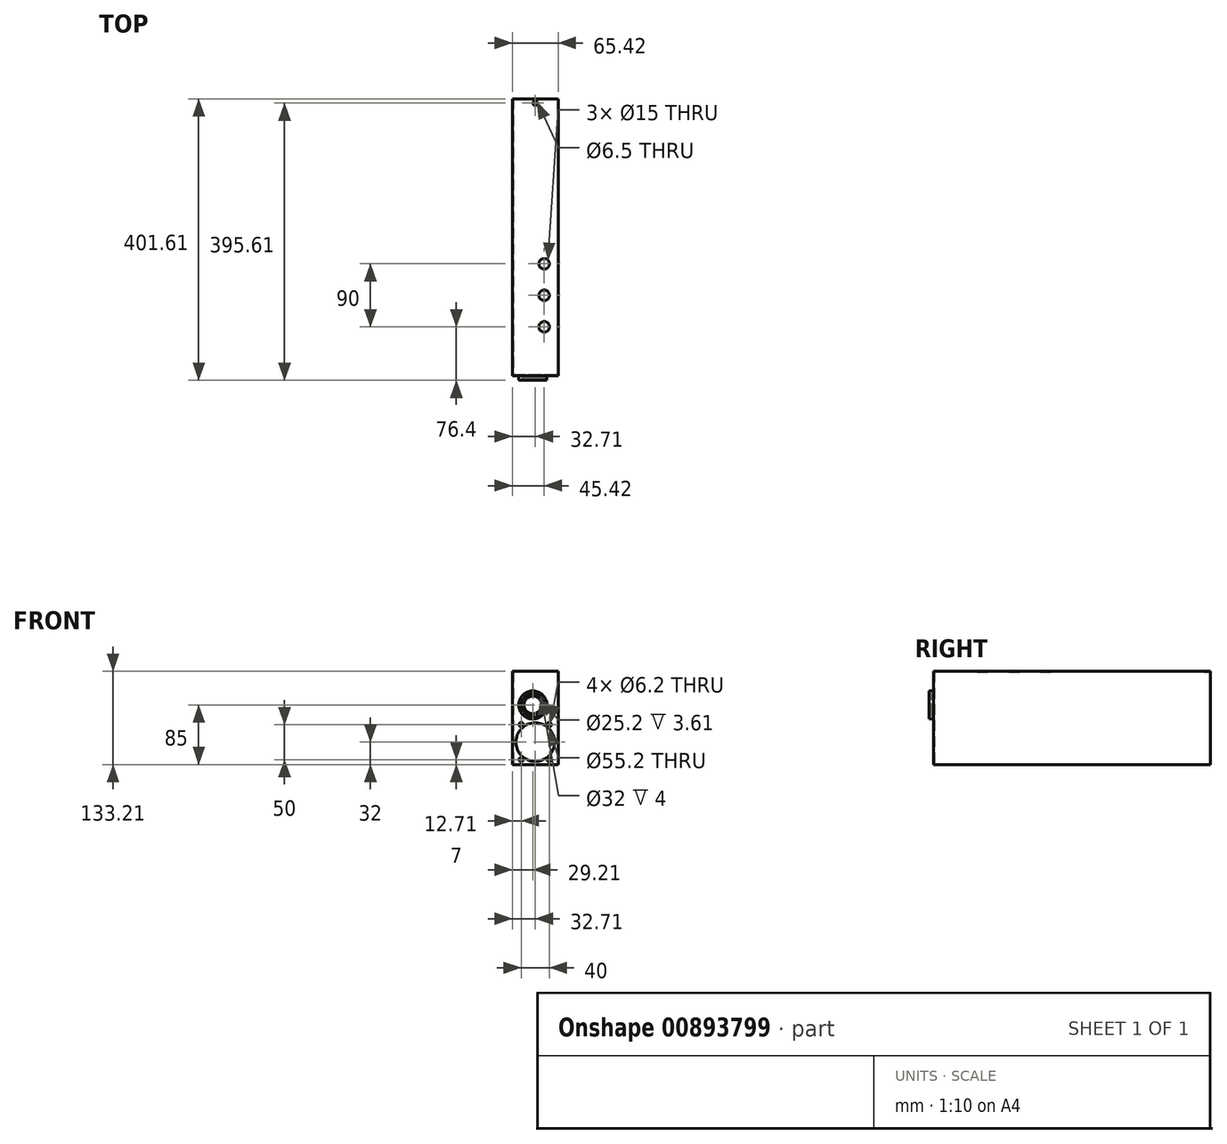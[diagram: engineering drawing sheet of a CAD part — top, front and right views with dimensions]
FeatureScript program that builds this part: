
annotation { "Feature Type Name" : "Feature", "Feature Type Description" : "" }
export const myFeature = defineFeature(function(context is Context, id is Id, definition is map)
    precondition{}
    {
        {
            var Q0;
            Q0=qCreatedBy(makeId("Front.planeOp"),FACE);
            var sketch = newSketch(context, id + "F0", { "sketchPlane" : qUnion([Q0])});
            skLineSegment(sketch, "E0", {"start": v(0, 132) * mm, "end": v(-31.5, 132) * mm});
            skLineSegment(sketch, "E1", {"start": v(-31.5, 132) * mm, "end": v(-31.5, 0) * mm});
            skLineSegment(sketch, "E2", {"start": v(-31.5, 0) * mm, "end": v(-32.7, 0) * mm});
            skLineSegment(sketch, "E3", {"start": v(-32.7, 0) * mm, "end": v(-32.7, 133.21) * mm});
            skLineSegment(sketch, "E4", {"start": v(-32.7, 133.21) * mm, "end": v(0, 133.21) * mm});
            skLineSegment(sketch, "E5", {"start": v(0, 30.11) * mm, "end": v(0, -5.7) * mm, "construction": true});
            skLineSegment(sketch, "E6.MirrorCS", {"start": v(31.5, 0) * mm, "end": v(32.7, 0) * mm});
            skLineSegment(sketch, "E7.MirrorCS", {"start": v(0, 132) * mm, "end": v(31.5, 132) * mm});
            skLineSegment(sketch, "E8.MirrorCS", {"start": v(31.5, 132) * mm, "end": v(31.5, 0) * mm});
            skLineSegment(sketch, "E9.MirrorCS", {"start": v(32.7, 133.21) * mm, "end": v(0, 133.21) * mm});
            skLineSegment(sketch, "E10.MirrorCS", {"start": v(32.7, 0) * mm, "end": v(32.7, 133.21) * mm});
            skSolve(sketch);
        }
        {
            var Q0;
            Q0 = qSketchRegion(id + "F0", true);
            extrude(context, id + "F1", {"entities" : qUnion([Q0]), "oppositeDirection" : true, "depth" : (394) * mm, "offsetDistance" : 25 * mm});
        }
        {
            var Q0;
            Q0=makeQuery(id+"F1.opExtrude","CAP_FACE",FACE,{"disambiguationData":[OSD([sQuery(id+"F0.wireOp",EDGE,"E0"),sQuery(id+"F0.wireOp",EDGE,"E1"),sQuery(id+"F0.wireOp",EDGE,"E2"),sQuery(id+"F0.wireOp",EDGE,"E3"),sQuery(id+"F0.wireOp",EDGE,"E4"),sQuery(id+"F0.wireOp",EDGE,"E6.MirrorCS"),sQuery(id+"F0.wireOp",EDGE,"E7.MirrorCS"),sQuery(id+"F0.wireOp",EDGE,"E8.MirrorCS"),sQuery(id+"F0.wireOp",EDGE,"E9.MirrorCS"),sQuery(id+"F0.wireOp",EDGE,"E10.MirrorCS")])],"isStart":true});
            var sketch = newSketch(context, id + "F2", { "sketchPlane" : qUnion([Q0])});
            skLineSegment(sketch, "E11.0", {"start": v(32.71, 0) * mm, "end": v(-32.7, 0) * mm});
            skLineSegment(sketch, "E12.0", {"start": v(-32.7, 0) * mm, "end": v(-32.7, 133.21) * mm});
            skLineSegment(sketch, "E13.0", {"start": v(32.7, 133.21) * mm, "end": v(-32.7, 133.21) * mm});
            skLineSegment(sketch, "E14.0", {"start": v(32.7, 0) * mm, "end": v(32.7, 133.21) * mm});
            skPoint(sketch, "E15.orphan", {"position": v(-31.5, 0) * mm});
            skSolve(sketch);
        }
        {
            var Q0;
            Q0 = qSketchRegion(id + "F2", true);
            extrude(context, id + "F3", {"entities" : qUnion([Q0]), "operationType" : NewBodyOperationType.ADD, "depth" : 1.21 * mm, "offsetDistance" : 25 * mm});
        }
        {
            var Q0;
            Q0=makeQuery(id+"F3.opExtrude","CAP_FACE",FACE,{"disambiguationData":[OSD([sQuery(id+"F2.wireOp",EDGE,"E11.0"),sQuery(id+"F2.wireOp",EDGE,"E12.0"),sQuery(id+"F2.wireOp",EDGE,"E13.0"),sQuery(id+"F2.wireOp",EDGE,"E14.0")])],"isStart":false});
            var sketch = newSketch(context, id + "F4", { "sketchPlane" : qUnion([Q0])});
            skCircle(sketch, "E16", {"center": v(0, 32) * mm, "radius": 27.6 * mm});
            skSolve(sketch);
        }
        {
            var Q0;
            Q0 = qSketchRegion(id + "F4", true);
            extrude(context, id + "F5", {"entities" : qUnion([Q0]), "operationType" : NewBodyOperationType.REMOVE, "endBound" : BoundingType.THROUGH_ALL, "oppositeDirection" : true, "depth" : 25 * mm, "offsetDistance" : 25 * mm});
        }
        {
            var Q0;
            Q0=makeQuery(id+"F3.opExtrude","CAP_FACE",FACE,{"disambiguationData":[OSD([sQuery(id+"F2.wireOp",EDGE,"E11.0"),sQuery(id+"F2.wireOp",EDGE,"E12.0"),sQuery(id+"F2.wireOp",EDGE,"E13.0"),sQuery(id+"F2.wireOp",EDGE,"E14.0")])],"isStart":false});
            var sketch = newSketch(context, id + "F6", { "sketchPlane" : qUnion([Q0])});
            skCircle(sketch, "E17", {"center": v(-3.5, 85) * mm, "radius": 12.6 * mm});
            skPoint(sketch, "E17.centerSnap0", {"position": v(0, 133.21) * mm});
            skCircle(sketch, "E18.0", {"center": v(0, 32) * mm, "radius": 27.6 * mm, "construction": true});
            skSolve(sketch);
        }
        {
            var Q0;
            Q0 = qSketchRegion(id + "F6", true);
            extrude(context, id + "F7", {"entities" : qUnion([Q0]), "operationType" : NewBodyOperationType.REMOVE, "endBound" : BoundingType.THROUGH_ALL, "oppositeDirection" : true, "depth" : 25 * mm, "offsetDistance" : 25 * mm, "hasSecondDirection" : true, "secondDirectionBound" : SecondDirectionBoundingType.THROUGH_ALL, "secondDirectionOppositeDirection" : false, "secondDirectionDepth" : 25 * mm});
        }
        {
            var Q0;
            Q0=makeQuery(id+"F3.opExtrude","CAP_FACE",FACE,{"disambiguationData":[OSD([sQuery(id+"F2.wireOp",EDGE,"E11.0"),sQuery(id+"F2.wireOp",EDGE,"E12.0"),sQuery(id+"F2.wireOp",EDGE,"E13.0"),sQuery(id+"F2.wireOp",EDGE,"E14.0")])],"isStart":false});
            var sketch = newSketch(context, id + "F8", { "sketchPlane" : qUnion([Q0])});
            skCircle(sketch, "E19.0", {"center": v(-3.5, 85) * mm, "radius": 12.6 * mm});
            skCircle(sketch, "E20", {"center": v(-3.5, 85) * mm, "radius": 20 * mm});
            skSolve(sketch);
        }
        {
            var Q0;
            Q0 = qSketchRegion(id + "F8", true);
            extrude(context, id + "F9", {"entities" : qUnion([Q0]), "operationType" : NewBodyOperationType.ADD, "depth" : 6.4 * mm, "offsetDistance" : 25 * mm});
        }
        {
            var Q0;
            Q0=makeQuery(id+"F9.opExtrude","CAP_FACE",FACE,{"disambiguationData":[OSD([sQuery(id+"F8.wireOp",EDGE,"E19.0"),sQuery(id+"F8.wireOp",EDGE,"E20")])],"isStart":false});
            var sketch = newSketch(context, id + "F10", { "sketchPlane" : qUnion([Q0])});
            skCircle(sketch, "E21", {"center": v(-3.5, 85) * mm, "radius": 16 * mm});
            skSolve(sketch);
        }
        {
            var Q0;
            Q0=makeQuery(id+"F3.boolean.opBoolean","MERGE",FACE,{"derivedFrom":[makeQuery(id+"F1.opExtrude","SWEPT_FACE",FACE,{"disambiguationData":[OSD([sQuery(id+"F0.wireOp",EDGE,"E4"),sQuery(id+"F0.wireOp",EDGE,"E9.MirrorCS")])]}),makeQuery(id+"F3.opExtrude","SWEPT_FACE",FACE,{"disambiguationData":[OSD([sQuery(id+"F2.wireOp",EDGE,"E13.0")])]})]});
            var sketch = newSketch(context, id + "F11", { "sketchPlane" : qUnion([Q0])});
            skCircle(sketch, "E22", {"center": v(12.7, 68.8) * mm, "radius": 7.5 * mm});
            skCircle(sketch, "E23", {"center": v(12.7, 113.8) * mm, "radius": 7.5 * mm});
            skCircle(sketch, "E24", {"center": v(12.7, 158.79) * mm, "radius": 7.5 * mm});
            skSolve(sketch);
        }
        {
            var Q0;
            Q0 = qSketchRegion(id + "F11", true);
            extrude(context, id + "F12", {"entities" : qUnion([Q0]), "operationType" : NewBodyOperationType.REMOVE, "endBound" : BoundingType.THROUGH_ALL, "oppositeDirection" : true, "depth" : 25 * mm, "offsetDistance" : 25 * mm});
        }
        {
            var Q0;
            Q0=makeQuery(id+"F3.boolean.opBoolean","MERGE",FACE,{"derivedFrom":[makeQuery(id+"F1.opExtrude","SWEPT_FACE",FACE,{"disambiguationData":[OSD([sQuery(id+"F0.wireOp",EDGE,"E4"),sQuery(id+"F0.wireOp",EDGE,"E9.MirrorCS")])]}),makeQuery(id+"F3.opExtrude","SWEPT_FACE",FACE,{"disambiguationData":[OSD([sQuery(id+"F2.wireOp",EDGE,"E13.0")])]})]});
            var sketch = newSketch(context, id + "F13", { "sketchPlane" : qUnion([Q0])});
            skCircle(sketch, "E25", {"center": v(0, 388) * mm, "radius": 3.25 * mm});
            skLineSegment(sketch, "E26", {"start": v(0, 0) * mm, "end": v(0, 401.41) * mm, "construction": true});
            skSolve(sketch);
        }
        {
            var Q0;
            Q0 = qSketchRegion(id + "F13", true);
            extrude(context, id + "F14", {"entities" : qUnion([Q0]), "operationType" : NewBodyOperationType.REMOVE, "oppositeDirection" : true, "depth" : 25 * mm, "offsetDistance" : 25 * mm});
        }
        {
            var Q0;
            Q0 = qSketchRegion(id + "F10", true);
            extrude(context, id + "F15", {"entities" : qUnion([Q0]), "operationType" : NewBodyOperationType.REMOVE, "oppositeDirection" : true, "depth" : 4 * mm, "offsetDistance" : 25 * mm});
        }
        {
            var Q0;
            Q0=makeQuery(id+"F8.imprint","IMPRINT",FACE,{"disambiguationData":[TD([[makeQuery(id+"F8.imprint","IMPRINT",EDGE,{"derivedFrom":sQuery(id+"F8.wireOp",EDGE,"E20")}),-1.0]])]});
            var sketch = newSketch(context, id + "F16", { "sketchPlane" : qUnion([Q0])});
            skCircle(sketch, "E27", {"center": v(20, 57) * mm, "radius": 3.1 * mm});
            skCircle(sketch, "E28", {"center": v(-20, 57) * mm, "radius": 3.1 * mm});
            skCircle(sketch, "E29", {"center": v(-20, 7) * mm, "radius": 3.1 * mm});
            skCircle(sketch, "E30", {"center": v(20, 7) * mm, "radius": 3.1 * mm});
            skCircle(sketch, "E31.0", {"center": v(0, 32) * mm, "radius": 27.6 * mm, "construction": true});
            skLineSegment(sketch, "E32", {"start": v(0, 67.38) * mm, "end": v(0, -3.38) * mm, "construction": true});
            skLineSegment(sketch, "E33", {"start": v(-38.94, 32) * mm, "end": v(38.94, 32) * mm, "construction": true});
            skSolve(sketch);
        }
        {
            var Q0;
            Q0 = qSketchRegion(id + "F16", true);
            extrude(context, id + "F17", {"entities" : qUnion([Q0]), "operationType" : NewBodyOperationType.REMOVE, "endBound" : BoundingType.THROUGH_ALL, "oppositeDirection" : true, "depth" : 25 * mm, "offsetDistance" : 25 * mm});
        }
    });
